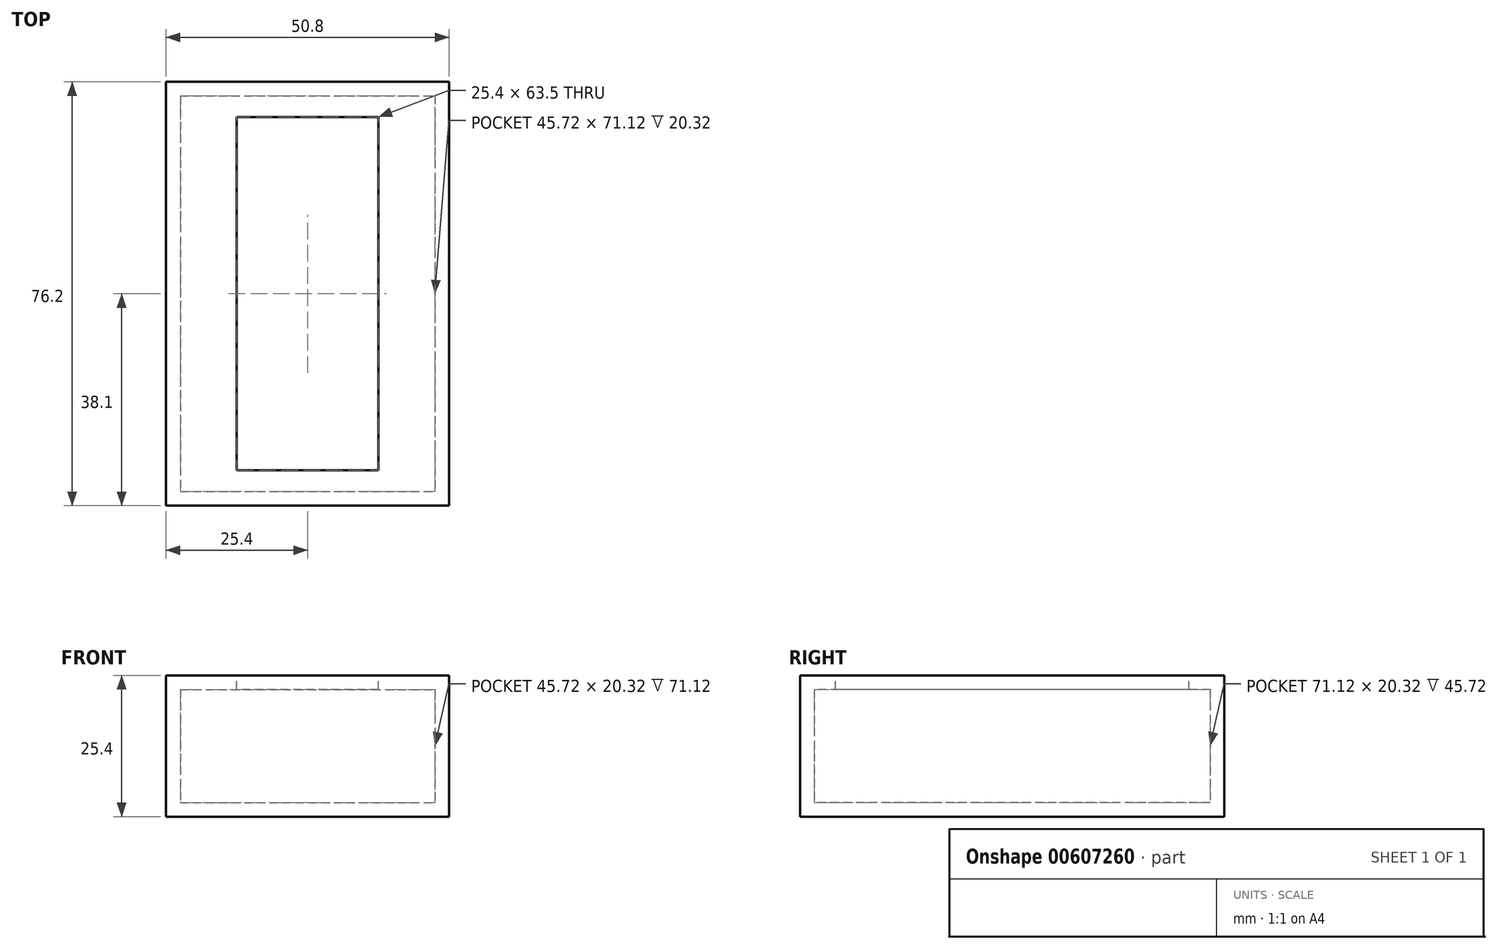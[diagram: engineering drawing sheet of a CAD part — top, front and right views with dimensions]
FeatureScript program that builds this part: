
annotation { "Feature Type Name" : "Feature", "Feature Type Description" : "" }
export const myFeature = defineFeature(function(context is Context, id is Id, definition is map)
    precondition{}
    {
        {
            var Q0;
            Q0=qCreatedBy(makeId("Top.planeOp"),FACE);
            var sketch = newSketch(context, id + "F0", { "sketchPlane" : qUnion([Q0])});
            skLineSegment(sketch, "E0.bottom", {"start": v(-25.4, 38.1) * mm, "end": v(25.4, 38.1) * mm});
            skLineSegment(sketch, "E0.top", {"start": v(-25.4, -38.1) * mm, "end": v(25.4, -38.1) * mm});
            skLineSegment(sketch, "E0.left", {"start": v(-25.4, 38.1) * mm, "end": v(-25.4, -38.1) * mm});
            skLineSegment(sketch, "E0.right", {"start": v(25.4, 38.1) * mm, "end": v(25.4, -38.1) * mm});
            skLineSegment(sketch, "E1.left", {"start": v(25.4, 38.1) * mm, "end": v(25.4, 38.1) * mm});
            skSolve(sketch);
        }
        {
            var Q0;
            Q0=makeQuery(id+"F0.imprint","IMPRINT",FACE,{"disambiguationData":[TD([[makeQuery(id+"F0.imprint","IMPRINT",EDGE,{"derivedFrom":sQuery(id+"F0.wireOp",EDGE,"E0.bottom")}),-1.0]])]});
            extrude(context, id + "F1", {"entities" : qUnion([Q0]), "depth" : 25.4 * mm, "offsetDistance" : 25.4 * mm});
        }
        {
            var Q0;
            Q0=makeQuery(id+"F1.opExtrude","CAP_FACE",FACE,{"disambiguationData":[OSD([sQuery(id+"F0.wireOp",EDGE,"E0.bottom"),sQuery(id+"F0.wireOp",EDGE,"E0.top"),sQuery(id+"F0.wireOp",EDGE,"E0.left"),sQuery(id+"F0.wireOp",EDGE,"E0.right")])],"isStart":false});
            var sketch = newSketch(context, id + "F2", { "sketchPlane" : qUnion([Q0])});
            skLineSegment(sketch, "E2.bottom", {"start": v(12.7, 31.75) * mm, "end": v(-12.7, 31.75) * mm});
            skLineSegment(sketch, "E2.top", {"start": v(12.7, -31.75) * mm, "end": v(-12.7, -31.75) * mm});
            skLineSegment(sketch, "E2.left", {"start": v(12.7, 31.75) * mm, "end": v(12.7, -31.75) * mm});
            skLineSegment(sketch, "E2.right", {"start": v(-12.7, 31.75) * mm, "end": v(-12.7, -31.75) * mm});
            skSolve(sketch);
        }
        {
            var Q0;
            Q0 = qSketchRegion(id + "F2", true);
            extrude(context, id + "F3", {"entities" : qUnion([Q0]), "operationType" : NewBodyOperationType.REMOVE, "oppositeDirection" : true, "depth" : 12.7 * mm, "offsetDistance" : 25.4 * mm});
        }
        {
            var Q0;
            Q0=makeQuery(id+"F3.boolean.opBoolean","COPY",FACE,{"derivedFrom":makeQuery(id+"F3.opExtrude","SWEPT_FACE",FACE,{"disambiguationData":[OSD([sQuery(id+"F2.wireOp",EDGE,"E2.right")])]})});
            var Q1;
            Q1=makeQuery(id+"F3.boolean.opBoolean","COPY",FACE,{"derivedFrom":makeQuery(id+"F3.opExtrude","CAP_FACE",FACE,{"disambiguationData":[OSD([sQuery(id+"F2.wireOp",EDGE,"E2.bottom"),sQuery(id+"F2.wireOp",EDGE,"E2.top"),sQuery(id+"F2.wireOp",EDGE,"E2.left"),sQuery(id+"F2.wireOp",EDGE,"E2.right")])],"isStart":false})});
            var Q2;
            Q2=makeQuery(id+"F3.boolean.opBoolean","COPY",FACE,{"derivedFrom":makeQuery(id+"F3.opExtrude","SWEPT_FACE",FACE,{"disambiguationData":[OSD([sQuery(id+"F2.wireOp",EDGE,"E2.bottom")])]})});
            var Q3;
            Q3=makeQuery(id+"F3.boolean.opBoolean","COPY",FACE,{"derivedFrom":makeQuery(id+"F3.opExtrude","SWEPT_FACE",FACE,{"disambiguationData":[OSD([sQuery(id+"F2.wireOp",EDGE,"E2.left")])]})});
            var Q4;
            Q4=makeQuery(id+"F3.boolean.opBoolean","COPY",FACE,{"derivedFrom":makeQuery(id+"F3.opExtrude","SWEPT_FACE",FACE,{"disambiguationData":[OSD([sQuery(id+"F2.wireOp",EDGE,"E2.top")])]})});
            shell(context, id + "F4", {"entities" : qUnion([Q0, Q1, Q2, Q3, Q4]), "thickness" : 2.54 * mm});
        }
    });
